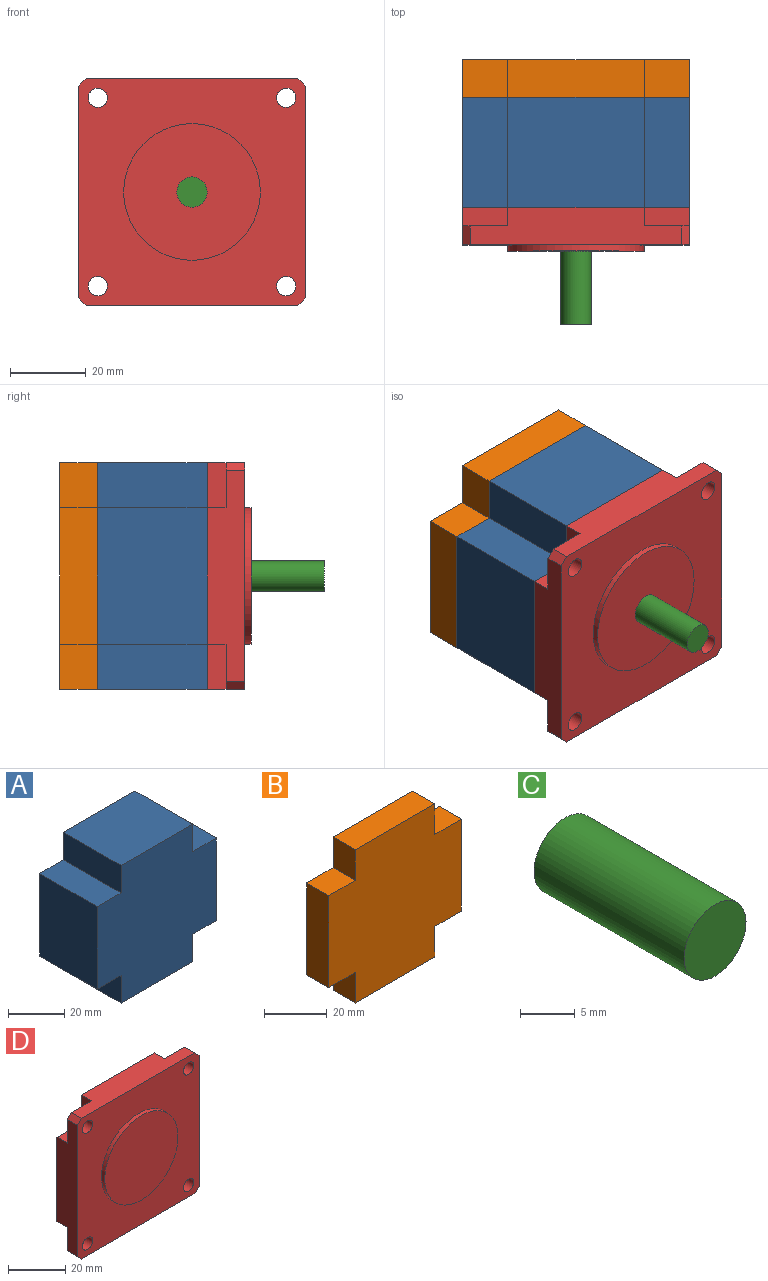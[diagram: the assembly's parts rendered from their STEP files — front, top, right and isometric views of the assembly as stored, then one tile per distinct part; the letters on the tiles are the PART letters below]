
ASSEMBLY  parts=4 mates=3
PART A: 14 faces, bbox 60x29x60 mm
  f0: plane 29x12mm, normal (0,0,1), area 348mm2, adj f1,f11,f12,f13
  f1: plane 36x29mm, normal (1,0,0), area 1044mm2, adj f0,f2,f12,f13
  f2: plane 29x12mm, normal (0,0,-1), area 348mm2, adj f1,f3,f12,f13
  f3: plane 29x12mm, normal (1,0,0), area 348mm2, adj f2,f4,f12,f13
  f4: plane 36x29mm, normal (0,0,-1), area 1044mm2, adj f3,f5,f12,f13
  f5: plane 29x12mm, normal (-1,0,0), area 348mm2, adj f4,f6,f12,f13
  f6: plane 29x12mm, normal (0,0,-1), area 348mm2, adj f5,f7,f12,f13
  f7: plane 36x29mm, normal (-1,0,0), area 1044mm2, adj f6,f8,f12,f13
  f8: plane 29x12mm, normal (0,0,1), area 348mm2, adj f7,f9,f12,f13
  f9: plane 29x12mm, normal (-1,0,0), area 348mm2, adj f8,f10,f12,f13
  f10: plane 36x29mm, normal (0,0,1), area 1044mm2, adj f9,f11,f12,f13
  f11: plane 29x12mm, normal (1,0,0), area 348mm2, adj f0,f10,f12,f13
  f12: plane 60x60mm, normal (0,1,0), area 3024mm2, adj f0,f1,f2,f3,f4,f5,f6,f7
  f13: plane 60x60mm, normal (0,-1,0), area 3024mm2, adj f0,f1,f2,f3,f4,f5,f6,f7
PART B: 14 faces, bbox 60x10x60 mm
  f0: plane 12x10mm, normal (0,0,1), area 120mm2, adj f1,f11,f12,f13
  f1: plane 36x10mm, normal (1,0,0), area 360mm2, adj f0,f2,f12,f13
  f2: plane 12x10mm, normal (0,0,-1), area 120mm2, adj f1,f3,f12,f13
  f3: plane 12x10mm, normal (1,0,0), area 120mm2, adj f2,f4,f12,f13
  f4: plane 36x10mm, normal (0,0,-1), area 360mm2, adj f3,f5,f12,f13
  f5: plane 12x10mm, normal (-1,0,0), area 120mm2, adj f4,f6,f12,f13
  f6: plane 12x10mm, normal (0,0,-1), area 120mm2, adj f5,f7,f12,f13
  f7: plane 36x10mm, normal (-1,0,0), area 360mm2, adj f6,f8,f12,f13
  f8: plane 12x10mm, normal (0,0,1), area 120mm2, adj f7,f9,f12,f13
  f9: plane 12x10mm, normal (-1,0,0), area 120mm2, adj f8,f10,f12,f13
  f10: plane 36x10mm, normal (0,0,1), area 360mm2, adj f9,f11,f12,f13
  f11: plane 12x10mm, normal (1,0,0), area 120mm2, adj f0,f10,f12,f13
  f12: plane 60x60mm, normal (0,1,0), area 3024mm2, adj f0,f1,f2,f3,f4,f5,f6,f7
  f13: plane 60x60mm, normal (0,-1,0), area 3024mm2, adj f0,f1,f2,f3,f4,f5,f6,f7
PART C: 3 faces, bbox 8x19.4x8 mm
  f0: cylinder r=4mm len=19.4mm, axis (0,1,0), area 487.6mm2, adj f1,f2
  f1: plane 8x8mm, normal (0,-1,0), area 50.3mm2, adj f0
  f2: plane 8x8mm, normal (0,1,0), area 50.3mm2, adj f0
PART D: 28 faces, bbox 60x11.6x60 mm
  f0: plane 12x12mm, normal (0,1,0), area 121.6mm2, adj f3,f4,f5,f13,f24,f25
  f1: plane 12x12mm, normal (0,1,0), area 121.6mm2, adj f3,f9,f10,f14,f19,f26
  f2: plane 12x12mm, normal (0,1,0), area 121.6mm2, adj f7,f8,f9,f15,f20,f21
  f3: plane 56x10mm, normal (0,0,1), area 460mm2, adj f0,f1,f4,f10,f11,f25,f26,f27
  f4: plane 5x2mm, normal (-0.71,0,0.71), area 14.1mm2, adj f0,f3,f5,f11
  f5: plane 56x10mm, normal (-1,0,0), area 460mm2, adj f0,f4,f6,f11,f12,f23,f24,f27
  f6: plane 5x2mm, normal (-0.71,0,-0.71), area 14.1mm2, adj f5,f7,f11,f12
  f7: plane 56x10mm, normal (0,0,-1), area 460mm2, adj f2,f6,f8,f11,f12,f21,f22,f27
  f8: plane 5x2mm, normal (0.71,0,-0.71), area 14.1mm2, adj f2,f7,f9,f11
  f9: plane 56x10mm, normal (1,0,0), area 460mm2, adj f1,f2,f8,f10,f11,f19,f20,f27
  f10: plane 5x2mm, normal (0.71,0,0.71), area 14.1mm2, adj f1,f3,f9,f11
  f11: plane 60x60mm, normal (0,-1,0), area 2486.7mm2, adj f3,f4,f5,f6,f7,f8,f9,f10
  f12: plane 12x12mm, normal (0,1,0), area 121.6mm2, adj f5,f6,f7,f16,f22,f23
  f13: cylinder r=2.55mm len=5.1mm, axis (0,-1,0), area 80.1mm2, adj f0,f11
  f14: cylinder r=2.55mm len=5.1mm, axis (0,-1,0), area 80.1mm2, adj f1,f11
  f15: cylinder r=2.55mm len=5.1mm, axis (0,-1,0), area 80.1mm2, adj f2,f11
  f16: cylinder r=2.55mm len=5.1mm, axis (0,-1,0), area 80.1mm2, adj f11,f12
  f17: cylinder r=18.05mm len=36.1mm, axis (0,1,0), area 181.5mm2, adj f11,f18
  f18: plane 36.1x36.1mm, normal (0,-1,0), area 1023.5mm2, adj f17
  f19: plane 12x5mm, normal (0,0,1), area 60mm2, adj f1,f9,f26,f27
  f20: plane 12x5mm, normal (0,0,-1), area 60mm2, adj f2,f9,f21,f27
  f21: plane 12x5mm, normal (1,0,0), area 60mm2, adj f2,f7,f20,f27
  f22: plane 12x5mm, normal (-1,0,0), area 60mm2, adj f7,f12,f23,f27
  f23: plane 12x5mm, normal (0,0,-1), area 60mm2, adj f5,f12,f22,f27
  f24: plane 12x5mm, normal (0,0,1), area 60mm2, adj f0,f5,f25,f27
  f25: plane 12x5mm, normal (-1,0,0), area 60mm2, adj f0,f3,f24,f27
  f26: plane 12x5mm, normal (1,0,0), area 60mm2, adj f1,f3,f19,f27
  f27: plane 60x60mm, normal (0,1,0), area 3024mm2, adj f3,f5,f7,f9,f19,f20,f21,f22
PLACE A at identity
PLACE B at identity
PLACE C at identity
PLACE D at identity
MATE fastened D.f27 <-> A.f13  axis (0,-1,0) through (18,5,30)mm
MATE fastened B.f13 <-> A.f12  axis (0,-1,0) through (18,34,30)mm
MATE fastened D.f17 <-> C.f0  axis (0,-1,0) through (0,-6.6,0)mm
